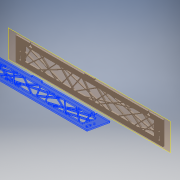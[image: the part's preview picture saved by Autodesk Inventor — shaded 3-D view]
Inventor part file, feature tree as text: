
AUTODESK INVENTOR PART (.ipt)
format: ipt  version: 2019 (Build 230136000, 136)  size: 1,171,968 bytes
history: native  units: in
note: dims shown in document units (in); Inventor stores cm internally (conversion verified against a paired STEP export)
features: fillet x10, other x9, extrude x8, reference x8, sketch x4, plane x1, hole x1
ambient origin geometry x8: Origin, YZ Plane, XZ Plane, XY Plane, X Axis, Y Axis, Z Axis, Center Point
bodies: Solid1 (feature_tree)
feature tree (41):
  plane  "Work Plane1"
  extrude  "FrontPanel"  Depth=0.0394in
  fillet  "CornerFillet"  Radius=0.475in
  extrude  "ScrewSlotExtrusion"  Depth=1.0in
  fillet  "ScrewSlotFillet"  Radius=0.3265in
  hole  "ScrewHoles"  [1 undecoded]
  extrude  "BottomTab"  Depth=0.3265in
  fillet  "BottomTabFillet"  Radius=0.1234in
  extrude  "Extrusion4"  Depth=1.0in
  fillet  "Fillet5"  Radius=0.125in
  extrude  "Extrusion5"  Depth=0.0197in
  fillet  "Fillet6"  Radius=0.1495in
  extrude  "Hash1"  Depth=1.0in
  extrude  "Hash2"  Depth=0.125in TaperAngle=0.0deg
  fillet  "GridFillets1"  Radius=0.0197in
  fillet  "GridFillets2"  Radius=0.429in
  fillet  "GridFillets3"  Radius=0.149in
  fillet  "GridFillets4"  Radius=0.429in
  fillet  "GridFillets5"  Radius=0.149in
  extrude  "FillSmallHoles"  Depth=0.125in TaperAngle=0.0deg
  sketch  "Sketch1"  dims[d0=0.125in d1=0.0in d3=0.0394in d4=0.475in]
  other  "ScrewSlotSketch"
  reference  "Reference1"
  reference  "Reference2"
  other  "ScrewHoleSketch"
  reference  "Reference3"
  reference  "Reference4"
  reference  "Reference5"
  reference  "Reference6"
  other  "BottomTabSketch"
  other  "SlotSketch"
  sketch  "Sketch6"  dims[d6=0.1495in d7=1.0in d8=0.3265in]
  reference  "Reference17"
  reference  "Reference18"
  sketch  "Sketch8"  dims[d9=0.1234in d10=0.1495in]
  sketch  "Sketch9"  dims[d11=0.475in d12=0.3265in d13=0.1234in d14=1.0in d19=0.125in d20=0.0in d21=0.0197in d22=0.1495in d23=0.75in d24=0.375in d25=0.25in d26=0.5635in d27=1.0in d28=0.8108in d29=1.0in d31=0.125in d32=0.0in d33=0.0197in d34=0.429in d36=0.149in d37=0.429in d38=0.149in d39=0.125in d40=0.0in d41=0.0197in d42=0.5in d43=0.5in d44=0.5in d45=0.5in d46=1.0in d47=0.0in d48=0.0197in d49=0.9256in d50=0.3306in d51=0.4953in d52=0.296in d53=0.4741in d54=1.1723in d55=0.928in d56=1.022in d57=2.0561in d58=1.1231in d59=3.0786in d60=1.0357in d61=4.6904in d62=0.9217in d63=5.6591in d64=1.0132in d65=7.399in d66=0.8542in d67=8.2469in d68=0.8705in d69=8.8513in d70=1.0501in d71=9.8758in d72=0.9174in d73=11.1086in d74=0.9517in d75=12.4209in d76=0.8283in d77=0.08in d78=0.08in d79=0.08in d80=0.08in d81=0.08in d82=0.08in d83=0.08in d84=0.08in d85=0.08in d86=0.08in d87=0.08in d88=0.08in d89=0.08in d90=0.08in d91=0.125in d92=0.0in d93=1.1219in d94=3.0408in d95=4.4555in d96=5.3985in d97=5.9142in d98=7.2919in d99=9.2854in d100=9.6146in d101=11.6521in d102=12.8869in d103=0.6025in d104=0.9919in d105=0.9726in d106=1.1441in d107=1.0602in d108=0.9366in d109=0.8777in d110=1.1106in d111=0.9193in d112=0.9535in d113=1.0843in d114=0.4761in d115=0.08in d116=0.08in d117=0.08in d118=0.08in d119=0.08in d120=0.08in d121=0.08in d122=0.08in d123=0.08in d124=0.08in d125=0.08in d126=0.125in d127=0.0in d128=0.0197in d129=0.0197in d130=0.0197in d131=0.0197in d132=0.0197in d133=0.125in d134=0.0in]
  parser-record x1  (decoder bookkeeping rows leaked as tree rows — omitted from the tree; the rows remain in map.json)
  other  "ArcadeController.iam"
  other  "Panel_side:1"
  other  "Panel_side:2"
  other  "BottomPanel:1"
note: 1 required parameter value undecoded (feature->parameter linkage not recoverable at this tier; creation-order binding heuristic only, values carry confidence <= 0.55)
note: 1 file-system path scrubbed to <path> (originals preserved in map.json)
